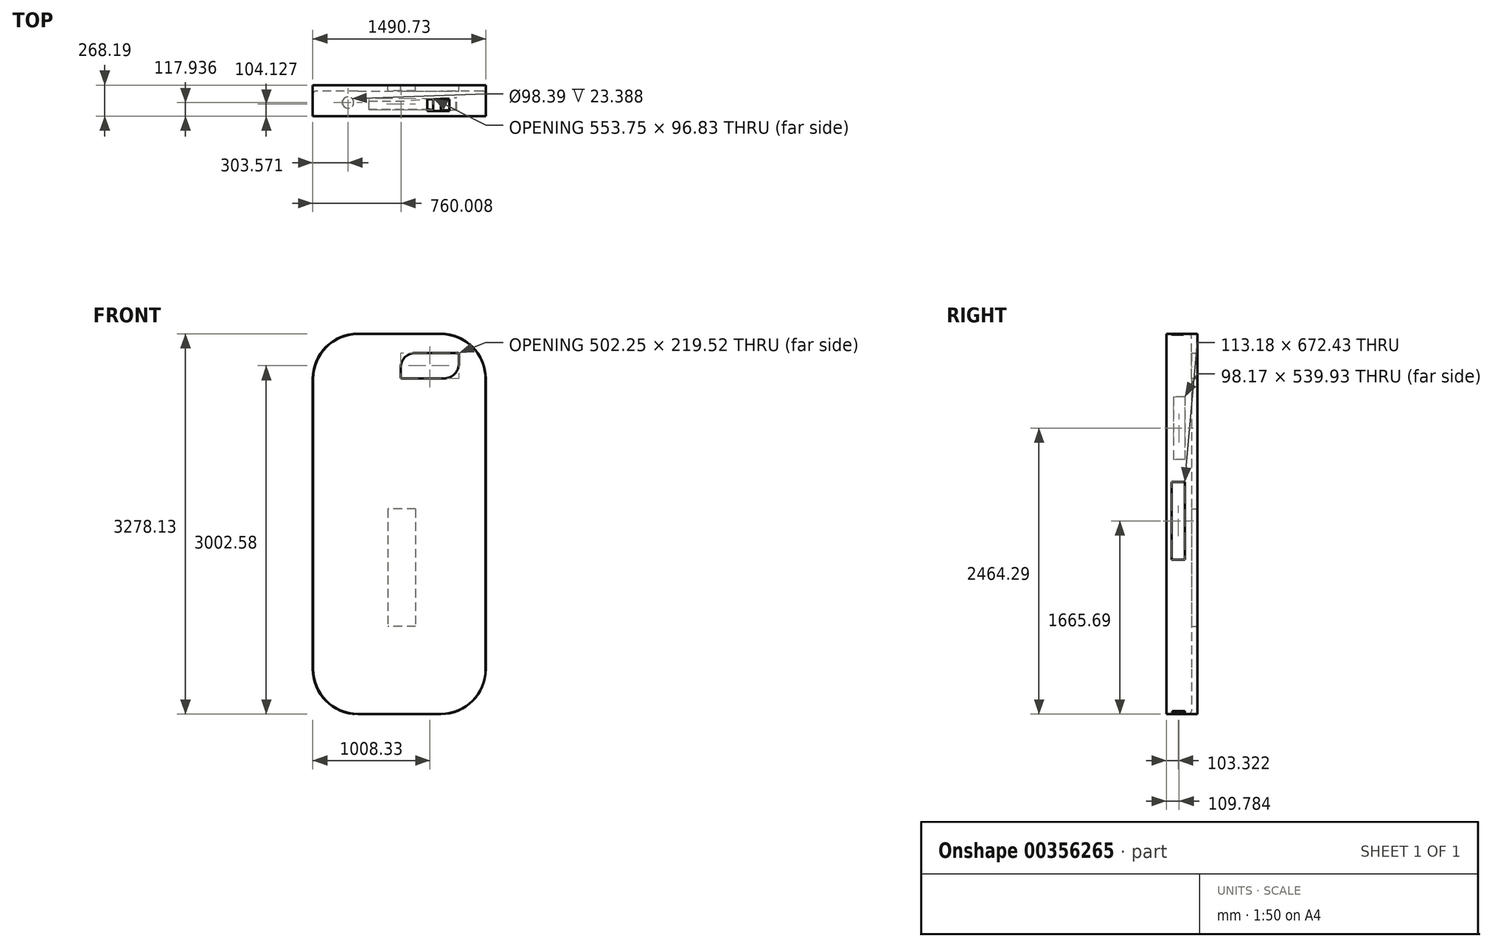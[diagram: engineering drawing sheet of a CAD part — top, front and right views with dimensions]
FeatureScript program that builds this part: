
annotation { "Feature Type Name" : "Feature", "Feature Type Description" : "" }
export const myFeature = defineFeature(function(context is Context, id is Id, definition is map)
    precondition{}
    {
        {
            var Q0;
            Q0=qCreatedBy(makeId("Front.planeOp"),FACE);
            var sketch = newSketch(context, id + "F0", { "sketchPlane" : qUnion([Q0])});
            skLineSegment(sketch, "E0.bottom", {"start": v(-369.09, 2072.74) * mm, "end": v(345.41, 2072.74) * mm});
            skLineSegment(sketch, "E0.top", {"start": v(-369.09, -1205.39) * mm, "end": v(345.41, -1205.39) * mm});
            skLineSegment(sketch, "E0.left", {"start": v(-757.2, 1684.62) * mm, "end": v(-757.2, -817.28) * mm});
            skLineSegment(sketch, "E0.right", {"start": v(733.53, 1684.62) * mm, "end": v(733.53, -817.28) * mm});
            skArc(sketch, "E1.filletArc", {"start": v(-369.09, 2072.74) * mm, "mid": v(-643.53, 1959.06) * mm, "end": v(-757.2, 1684.62) * mm});
            skPoint(sketch, "E2.visualSharp", {"position": v(733.53, 2072.74) * mm});
            skArc(sketch, "E2.filletArc", {"start": v(733.53, 1684.62) * mm, "mid": v(619.85, 1959.06) * mm, "end": v(345.41, 2072.74) * mm});
            skPoint(sketch, "E3.visualSharp", {"position": v(-757.2, -1205.39) * mm});
            skArc(sketch, "E3.filletArc", {"start": v(-757.2, -817.28) * mm, "mid": v(-643.53, -1091.71) * mm, "end": v(-369.09, -1205.39) * mm});
            skPoint(sketch, "E4.visualSharp", {"position": v(733.53, -1205.39) * mm});
            skArc(sketch, "E4.filletArc", {"start": v(345.41, -1205.39) * mm, "mid": v(619.85, -1091.71) * mm, "end": v(733.53, -817.28) * mm});
            skArc(sketch, "E5.0", {"start": v(-369.09, 2079.09) * mm, "mid": v(-648.02, 1963.55) * mm, "end": v(-763.55, 1684.62) * mm});
            skLineSegment(sketch, "E5.1", {"start": v(-369.09, 2079.09) * mm, "end": v(345.41, 2079.09) * mm});
            skLineSegment(sketch, "E5.2", {"start": v(-763.55, 1684.62) * mm, "end": v(-763.55, -817.28) * mm});
            skArc(sketch, "E5.3", {"start": v(739.88, 1684.62) * mm, "mid": v(624.34, 1963.55) * mm, "end": v(345.41, 2079.09) * mm});
            skArc(sketch, "E5.4", {"start": v(-763.55, -817.28) * mm, "mid": v(-648.02, -1096.2) * mm, "end": v(-369.09, -1211.74) * mm});
            skLineSegment(sketch, "E5.5", {"start": v(-369.09, -1211.74) * mm, "end": v(345.41, -1211.74) * mm});
            skArc(sketch, "E5.6", {"start": v(345.41, -1211.74) * mm, "mid": v(624.34, -1096.2) * mm, "end": v(739.88, -817.28) * mm});
            skLineSegment(sketch, "E5.7", {"start": v(739.88, 1684.62) * mm, "end": v(739.88, -817.28) * mm});
            skArc(sketch, "E6.0", {"start": v(-369.09, 2085.44) * mm, "mid": v(-652.5, 1968.04) * mm, "end": v(-769.9, 1684.62) * mm});
            skArc(sketch, "E7.0", {"start": v(746.23, 1684.62) * mm, "mid": v(628.83, 1968.04) * mm, "end": v(345.41, 2085.44) * mm});
            skSolve(sketch);
        }
        {
            var Q0;
            Q0=makeQuery(id+"F0.imprint","IMPRINT",FACE,{"disambiguationData":[TD([[makeQuery(id+"F0.imprint","IMPRINT",EDGE,{"derivedFrom":sQuery(id+"F0.wireOp",EDGE,"E0.bottom")}),-1.0]])]});
            extrude(context, id + "F1", {"entities" : qUnion([Q0]), "depth" : 218.2 * mm});
        }
        {
            var Q0;
            Q0=makeQuery(id+"F1.opExtrude","CAP_FACE",FACE,{"disambiguationData":[OSD([sQuery(id+"F0.wireOp",EDGE,"E0.bottom"),sQuery(id+"F0.wireOp",EDGE,"E0.top"),sQuery(id+"F0.wireOp",EDGE,"E0.left"),sQuery(id+"F0.wireOp",EDGE,"E0.right"),sQuery(id+"F0.wireOp",EDGE,"E1.filletArc"),sQuery(id+"F0.wireOp",EDGE,"E2.filletArc"),sQuery(id+"F0.wireOp",EDGE,"E3.filletArc"),sQuery(id+"F0.wireOp",EDGE,"E4.filletArc")])],"isStart":false});
            shell(context, id + "F2", {"entities" : qUnion([Q0]), "thickness" : 2 * mm});
        }
        {
            var Q0;
            {var subQ0=sQuery(id+"F0.wireOp",EDGE,"E0.right");Q0=makeQuery(id+"F2.opShell","OFFSET_EDGE",EDGE,{"disambiguationData":[OSD([subQ0]),TDD([makeQuery(id+"F1.opExtrude","CAP_EDGE",EDGE,{"disambiguationData":[OSD([subQ0])],"isStart":true})])]});}
            fillet(context, id + "F3", {"entities" : qUnion([Q0]), "radius" : 25.4 * mm, "tangentPropagation" : true, "allowEdgeOverflow" : false});
        }
        {
            var Q0;
            Q0=makeQuery(id+"F1.opExtrude","SWEPT_FACE",FACE,{"disambiguationData":[OSD([sQuery(id+"F0.wireOp",EDGE,"E0.left")])]});
            var sketch = newSketch(context, id + "F4", { "sketchPlane" : qUnion([Q0])});
            skLineSegment(sketch, "E8.bottom", {"start": v(59.32, 1528.87) * mm, "end": v(157.5, 1528.87) * mm});
            skLineSegment(sketch, "E8.top", {"start": v(59.32, 988.94) * mm, "end": v(157.5, 988.94) * mm});
            skLineSegment(sketch, "E8.left", {"start": v(59.32, 1528.87) * mm, "end": v(59.32, 988.94) * mm});
            skLineSegment(sketch, "E8.right", {"start": v(157.5, 1528.87) * mm, "end": v(157.5, 988.94) * mm});
            skSolve(sketch);
        }
        {
            var Q0;
            Q0=makeQuery(id+"F4.imprint","IMPRINT",FACE,{"disambiguationData":[TD([[makeQuery(id+"F4.imprint","IMPRINT",EDGE,{"derivedFrom":sQuery(id+"F4.wireOp",EDGE,"E8.bottom")}),-1.0]])]});
            extrude(context, id + "F5", {"entities" : qUnion([Q0]), "operationType" : NewBodyOperationType.REMOVE, "oppositeDirection" : true, "depth" : 25 * mm});
        }
        {
            var Q0;
            Q0=makeQuery(id+"F1.opExtrude","SWEPT_FACE",FACE,{"disambiguationData":[OSD([sQuery(id+"F0.wireOp",EDGE,"E0.bottom")])]});
            var sketch = newSketch(context, id + "F6", { "sketchPlane" : qUnion([Q0])});
            skLineSegment(sketch, "E9.bottom", {"start": v(419.43, -71.26) * mm, "end": v(230.36, -71.26) * mm});
            skLineSegment(sketch, "E9.top", {"start": v(419.43, -172.1) * mm, "end": v(230.36, -172.1) * mm});
            skLineSegment(sketch, "E9.left", {"start": v(419.43, -71.26) * mm, "end": v(419.43, -172.1) * mm});
            skLineSegment(sketch, "E9.right", {"start": v(230.36, -71.26) * mm, "end": v(230.36, -172.1) * mm});
            skSolve(sketch);
        }
        {
            var Q0;
            {var subQ0=sQuery(id+"F6.wireOp",EDGE,"E9.right");Q0=makeQuery(id+"F6.imprint","IMPRINT",FACE,{"disambiguationData":[TD([[makeQuery(id+"F6.imprint","IMPRINT",EDGE,{"derivedFrom":subQ0}),1.0]])]});}
            var Q1;
            {var subQ0=sQuery(id+"F6.wireOp",EDGE,"E9.left");Q1=makeQuery(id+"F6.imprint","IMPRINT",FACE,{"disambiguationData":[TD([[makeQuery(id+"F6.imprint","IMPRINT",EDGE,{"derivedFrom":subQ0}),-1.0]])]});}
            extrude(context, id + "F7", {"entities" : qUnion([Q0, Q1]), "operationType" : NewBodyOperationType.REMOVE, "oppositeDirection" : true, "depth" : 25 * mm});
        }
        {
            var Q0;
            Q0=makeQuery(id+"F1.opExtrude","SWEPT_FACE",FACE,{"disambiguationData":[OSD([sQuery(id+"F0.wireOp",EDGE,"E0.top")])]});
            var sketch = newSketch(context, id + "F8", { "sketchPlane" : qUnion([Q0])});
            skLineSegment(sketch, "E10", {"start": v(-274.07, 160.48) * mm, "end": v(-274.07, 88.05) * mm});
            skLineSegment(sketch, "E11", {"start": v(-274.07, 88.05) * mm, "end": v(254.64, 88.05) * mm});
            skLineSegment(sketch, "E12", {"start": v(254.64, 88.05) * mm, "end": v(254.64, 160.48) * mm});
            skLineSegment(sketch, "E13", {"start": v(254.64, 160.48) * mm, "end": v(-274.07, 160.48) * mm});
            skLineSegment(sketch, "E14", {"start": v(439.4, 167.72) * mm, "end": v(588.73, 167.72) * mm});
            skLineSegment(sketch, "E15", {"start": v(588.73, 167.72) * mm, "end": v(588.73, 59.08) * mm});
            skLineSegment(sketch, "E16", {"start": v(588.73, 59.08) * mm, "end": v(439.4, 59.08) * mm});
            skLineSegment(sketch, "E17", {"start": v(-274.07, 88.05) * mm, "end": v(-274.07, 27.7) * mm});
            skLineSegment(sketch, "E18", {"start": v(-274.07, 27.7) * mm, "end": v(259.32, 27.7) * mm});
            skLineSegment(sketch, "E19", {"start": v(259.32, 27.7) * mm, "end": v(254.64, 88.05) * mm});
            skLineSegment(sketch, "E20", {"start": v(439.4, 167.72) * mm, "end": v(345.41, 167.72) * mm});
            skLineSegment(sketch, "E21", {"start": v(439.4, 59.08) * mm, "end": v(345.41, 59.08) * mm});
            skLineSegment(sketch, "E22", {"start": v(345.41, 167.72) * mm, "end": v(254.64, 160.48) * mm});
            skLineSegment(sketch, "E23", {"start": v(345.41, 59.08) * mm, "end": v(55.47, 88.05) * mm});
            skLineSegment(sketch, "E24", {"start": v(279.69, 162.48) * mm, "end": v(279.69, 65.65) * mm});
            skCircle(sketch, "E25", {"center": v(-453.63, 100.25) * mm, "radius": 49.2 * mm});
            skSolve(sketch);
        }
        {
            var Q0;
            Q0=makeQuery(id+"F8.imprint","IMPRINT",FACE,{"disambiguationData":[TD([[makeQuery(id+"F8.imprint","IMPRINT",EDGE,{"derivedFrom":sQuery(id+"F8.wireOp",EDGE,"E11")}),-1.0]])]});
            var Q1;
            Q1=makeQuery(id+"F8.imprint","IMPRINT",FACE,{"disambiguationData":[TD([[makeQuery(id+"F8.imprint","IMPRINT",EDGE,{"derivedFrom":sQuery(id+"F8.wireOp",EDGE,"E10")}),1.0]])]});
            var Q2;
            Q2=makeQuery(id+"F8.imprint","IMPRINT",FACE,{"disambiguationData":[TD([[makeQuery(id+"F8.imprint","IMPRINT",EDGE,{"derivedFrom":sQuery(id+"F8.wireOp",EDGE,"W1eXPSfE-ctgO-CHkB-Q8A2-MUbmOAQsFZe9.bottom")}),-1.0]])]});
            var Q3;
            {var subQ2=sQuery(id+"F8.wireOp",EDGE,"E12");Q3=makeQuery(id+"F8.imprint","IMPRINT",FACE,{"disambiguationData":[TD([[makeQuery(id+"F8.imprint","IMPRINT",EDGE,{"derivedFrom":subQ2}),-1.0]])]});}
            var Q4;
            Q4=makeQuery(id+"F8.imprint","IMPRINT",FACE,{"disambiguationData":[TD([[makeQuery(id+"F8.imprint","IMPRINT",EDGE,{"derivedFrom":sQuery(id+"F8.wireOp",EDGE,"E14")}),-1.0]])]});
            var Q5;
            Q5=makeQuery(id+"F8.imprint","IMPRINT",FACE,{"disambiguationData":[TD([[makeQuery(id+"F8.imprint","IMPRINT",EDGE,{"derivedFrom":sQuery(id+"F8.wireOp",EDGE,"UwW7JBDX-PEKr-Xek4-TPsW-XtcPUK0sGrRT")}),1.0]])]});
            var Q6;
            Q6=makeQuery(id+"F8.imprint","IMPRINT",FACE,{"disambiguationData":[TD([[makeQuery(id+"F8.imprint","IMPRINT",EDGE,{"derivedFrom":sQuery(id+"F8.wireOp",EDGE,"E25")}),1.0]])]});
            extrude(context, id + "F9", {"entities" : qUnion([Q0, Q1, Q2, Q3, Q4, Q5, Q6]), "operationType" : NewBodyOperationType.REMOVE, "oppositeDirection" : true, "depth" : 25 * mm});
        }
        {
            var Q0;
            Q0=makeQuery(id+"F1.opExtrude","SWEPT_FACE",FACE,{"disambiguationData":[OSD([sQuery(id+"F0.wireOp",EDGE,"E0.right")])]});
            var sketch = newSketch(context, id + "F10", { "sketchPlane" : qUnion([Q0])});
            skLineSegment(sketch, "E26.bottom", {"start": v(-171.46, 796.52) * mm, "end": v(-58.28, 796.52) * mm});
            skLineSegment(sketch, "E26.top", {"start": v(-171.46, 124.1) * mm, "end": v(-58.28, 124.1) * mm});
            skLineSegment(sketch, "E26.left", {"start": v(-171.46, 796.52) * mm, "end": v(-171.46, 124.1) * mm});
            skLineSegment(sketch, "E26.right", {"start": v(-58.28, 796.52) * mm, "end": v(-58.28, 124.1) * mm});
            skSolve(sketch);
        }
        {
            var Q0;
            Q0=makeQuery(id+"F10.imprint","IMPRINT",FACE,{"disambiguationData":[TD([[makeQuery(id+"F10.imprint","IMPRINT",EDGE,{"derivedFrom":sQuery(id+"F10.wireOp",EDGE,"E26.bottom")}),-1.0]])]});
            extrude(context, id + "F11", {"entities" : qUnion([Q0]), "operationType" : NewBodyOperationType.REMOVE, "oppositeDirection" : true, "depth" : 25 * mm});
        }
        {
            var Q0;
            Q0=makeQuery(id+"F1.opExtrude","CAP_FACE",FACE,{"disambiguationData":[OSD([sQuery(id+"F0.wireOp",EDGE,"E0.bottom"),sQuery(id+"F0.wireOp",EDGE,"E0.top"),sQuery(id+"F0.wireOp",EDGE,"E0.left"),sQuery(id+"F0.wireOp",EDGE,"E0.right"),sQuery(id+"F0.wireOp",EDGE,"E1.filletArc"),sQuery(id+"F0.wireOp",EDGE,"E2.filletArc"),sQuery(id+"F0.wireOp",EDGE,"E3.filletArc"),sQuery(id+"F0.wireOp",EDGE,"E4.filletArc")])],"isStart":true});
            var sketch = newSketch(context, id + "F12", { "sketchPlane" : qUnion([Q0])});
            skSolve(sketch);
        }
        {
            var Q0;
            Q0=makeQuery(id+"F12.imprint","IMPRINT",FACE,{"disambiguationData":[TD([[makeQuery(id+"F12.imprint","IMPRINT",EDGE,{"derivedFrom":makeQuery(id+"F1.opExtrude","CAP_EDGE",EDGE,{"disambiguationData":[OSD([sQuery(id+"F0.wireOp",EDGE,"E0.bottom")])],"isStart":true})}),1.0]])]});
            var sketch = newSketch(context, id + "F13", { "sketchPlane" : qUnion([Q0])});
            skLineSegment(sketch, "E27.bottom", {"start": v(-492.25, 1906.95) * mm, "end": v(-123.96, 1906.95) * mm});
            skLineSegment(sketch, "E27.top", {"start": v(-371.31, 1687.43) * mm, "end": v(-10, 1687.43) * mm});
            skLineSegment(sketch, "E27.left", {"start": v(-502.25, 1896.95) * mm, "end": v(-502.25, 1818.38) * mm});
            skLineSegment(sketch, "E27.right", {"start": v(0, 1783) * mm, "end": v(0, 1697.43) * mm});
            skPoint(sketch, "E28.visualSharp", {"position": v(-502.25, 1906.95) * mm});
            skArc(sketch, "E28.filletArc", {"start": v(-492.25, 1906.95) * mm, "mid": v(-499.32, 1904.02) * mm, "end": v(-502.25, 1896.95) * mm});
            skPoint(sketch, "E29.visualSharp", {"position": v(-502.25, 1687.43) * mm});
            skArc(sketch, "E29.filletArc", {"start": v(-502.25, 1818.38) * mm, "mid": v(-463.9, 1725.78) * mm, "end": v(-371.31, 1687.43) * mm});
            skPoint(sketch, "E30.visualSharp", {"position": v(0, 1906.95) * mm});
            skArc(sketch, "E30.filletArc", {"start": v(0, 1783) * mm, "mid": v(-36.3, 1870.65) * mm, "end": v(-123.96, 1906.95) * mm});
            skPoint(sketch, "E31.visualSharp", {"position": v(0, 1687.43) * mm});
            skArc(sketch, "E31.filletArc", {"start": v(-10, 1687.43) * mm, "mid": v(-2.93, 1690.36) * mm, "end": v(0, 1697.43) * mm});
            skSolve(sketch);
        }
        {
            var Q0;
            Q0 = qSketchRegion(id + "F13", true);
            extrude(context, id + "F14", {"entities" : qUnion([Q0]), "operationType" : NewBodyOperationType.REMOVE, "oppositeDirection" : true, "depth" : 25 * mm});
        }
        {
            var Q0;
            Q0=makeQuery(id+"F12.imprint","IMPRINT",FACE,{"disambiguationData":[TD([[makeQuery(id+"F12.imprint","IMPRINT",EDGE,{"derivedFrom":makeQuery(id+"F1.opExtrude","CAP_EDGE",EDGE,{"disambiguationData":[OSD([sQuery(id+"F0.wireOp",EDGE,"E0.bottom")])],"isStart":true})}),1.0]])]});
            extrude(context, id + "F15", {"entities" : qUnion([Q0]), "operationType" : NewBodyOperationType.ADD, "depth" : 50 * mm});
        }
        {
            var Q0;
            Q0=makeQuery(id+"F15.opExtrude","CAP_FACE",FACE,{"disambiguationData":[OSD([sQuery(id+"F0.wireOp",EDGE,"E0.bottom"),sQuery(id+"F0.wireOp",EDGE,"E0.top"),sQuery(id+"F0.wireOp",EDGE,"E0.left"),sQuery(id+"F0.wireOp",EDGE,"E0.right"),sQuery(id+"F0.wireOp",EDGE,"E1.filletArc"),sQuery(id+"F0.wireOp",EDGE,"E2.filletArc"),sQuery(id+"F0.wireOp",EDGE,"E3.filletArc"),sQuery(id+"F0.wireOp",EDGE,"E4.filletArc")])],"isStart":true});
            extrude(context, id + "F16", {"entities" : qUnion([Q0]), "operationType" : NewBodyOperationType.REMOVE, "oppositeDirection" : true, "depth" : 115 * mm});
        }
        {
            var Q0;
            Q0=makeQuery(id+"F15.opExtrude","CAP_FACE",FACE,{"disambiguationData":[OSD([sQuery(id+"F0.wireOp",EDGE,"E0.bottom"),sQuery(id+"F0.wireOp",EDGE,"E0.top"),sQuery(id+"F0.wireOp",EDGE,"E0.left"),sQuery(id+"F0.wireOp",EDGE,"E0.right"),sQuery(id+"F0.wireOp",EDGE,"E1.filletArc"),sQuery(id+"F0.wireOp",EDGE,"E2.filletArc"),sQuery(id+"F0.wireOp",EDGE,"E3.filletArc"),sQuery(id+"F0.wireOp",EDGE,"E4.filletArc")])],"isStart":false});
            var sketch = newSketch(context, id + "F17", { "sketchPlane" : qUnion([Q0])});
            skLineSegment(sketch, "E32.bottom", {"start": v(-127.97, 563.5) * mm, "end": v(111.7, 563.5) * mm});
            skLineSegment(sketch, "E32.top", {"start": v(-127.97, -448.47) * mm, "end": v(111.7, -448.47) * mm});
            skLineSegment(sketch, "E32.left", {"start": v(-127.97, 563.5) * mm, "end": v(-127.97, -448.47) * mm});
            skLineSegment(sketch, "E32.right", {"start": v(111.7, 563.5) * mm, "end": v(111.7, -448.47) * mm});
            skSolve(sketch);
        }
        {
            var Q0;
            Q0 = qSketchRegion(id + "F17", true);
            extrude(context, id + "F18", {"entities" : qUnion([Q0]), "operationType" : NewBodyOperationType.REMOVE, "oppositeDirection" : true, "depth" : 50 * mm});
        }
    });
